# Revit family: 931-20-001 DN250-350
name_source: partatom
category: Pipe Accessories
units: mm (PartAtom-declared; Revit-internal decimal feet)

## family parameters
Always vertical = Yes
Cut with Voids When Loaded = No
Part Type = Valve - Breaks Into
Round Connector Dimension = Use Diameter
Shared = No
Work Plane-Based = No

## types (6) — shared parameters
1 = 1 mm  [stored 0.00328084 ft]
2 = 3 mm  [stored 0.00984252 ft]
DN250 PN10 = 931-250-20-010020200000
DN250 PN16 = 931-250-20-020020200000
DN300_PN10 = 931-300-20-010020200000
DN300_PN16 = 931-300-20-020020200000
DN350_PN10 = 931-350-20-010020200000
DN350_PN16 = 931-350-20-020020200000
Description_ = AVK BUTTERFLY VALVE, LUG, PN10/16
F = 32 mm  [stored 0.104987 ft]
Search_table = 931-20-001 DN250-350
Slot_dim = 19 mm  [stored 0.062336 ft]
URL_product_pages = https://www.avkvalves.com
zero-valued in all types: DISK, Default Elevation

## per-type parameters (varying)
- DN250 PN10: Actuator_FL_T=22 mm  [stored 0.0721785 ft]; Actuator_Flange_R=63 mm; B=125 mm; B1=126 mm; Body_Thickness=8 mm  [stored 0.0262467 ft]; Body_dim=31 mm  [stored 0.101706 ft]; Body_dim1=48 mm  [stored 0.15748 ft]; Body_thickness=132 mm; Bore_R=125 mm; C=68 mm  [stored 0.223097 ft]; D=165 mm; DN=250 mm; E=273 mm; Flange_R=200 mm; Flange_T=22 mm  [stored 0.0721785 ft]; G=22 mm  [stored 0.0721785 ft]; H=75 mm  [stored 0.246063 ft]; Hole=24 mm; Hole1=19 mm  [stored 0.062336 ft]; PCD_R=175 mm; base=24 mm; base1=14 mm  [stored 0.0459318 ft]; base_dis=195 mm; disk=11 mm  [stored 0.0360892 ft]; disk1=22 mm  [stored 0.0721785 ft]; disk11=29 mm  [stored 0.0951444 ft]; disk2=250 mm; disk22=14 mm  [stored 0.0459318 ft]; hole1=11 mm  [stored 0.0360892 ft]; logo=175 mm; rubber=20 mm  [stored 0.0656168 ft]; support=210 mm; wafer=94 mm; wafer_F=28 mm  [stored 0.0918635 ft]; wafer_dim1=31 mm  [stored 0.101706 ft]; wafer_dim2=86 mm  [stored 0.282152 ft]; wafer_fillet=47 mm
- DN250 PN16: Actuator_FL_T=20 mm  [stored 0.0656168 ft]; Actuator_Flange_R=63 mm; B=125 mm; B1=126 mm; Body_Thickness=8 mm  [stored 0.0262467 ft]; Body_dim=31 mm  [stored 0.101706 ft]; Body_dim1=48 mm  [stored 0.15748 ft]; Body_thickness=132 mm; Bore_R=125 mm; C=68 mm  [stored 0.223097 ft]; D=165 mm; DN=250 mm; E=273 mm; Flange_R=200 mm; Flange_T=20 mm  [stored 0.0656168 ft]; G=22 mm  [stored 0.0721785 ft]; H=75 mm  [stored 0.246063 ft]; Hole=24 mm; Hole1=19 mm  [stored 0.062336 ft]; PCD_R=178 mm; base=24 mm; base1=14 mm  [stored 0.0459318 ft]; base_dis=195 mm; disk=12 mm  [stored 0.0393701 ft]; disk1=22 mm  [stored 0.0721785 ft]; disk11=29 mm  [stored 0.0951444 ft]; disk2=250 mm; disk22=16 mm  [stored 0.0524934 ft]; hole1=11 mm  [stored 0.0360892 ft]; logo=175 mm; rubber=20 mm  [stored 0.0656168 ft]; support=210 mm; wafer=94 mm; wafer_F=28 mm  [stored 0.0918635 ft]; wafer_dim1=32 mm  [stored 0.104987 ft]; wafer_dim2=78 mm  [stored 0.255906 ft]; wafer_fillet=47 mm
- DN300_PN10: Actuator_FL_T=20 mm  [stored 0.0656168 ft]; Actuator_Flange_R=63 mm; B=150 mm; B1=151 mm; Body_Thickness=8 mm  [stored 0.0262467 ft]; Body_dim=31 mm  [stored 0.101706 ft]; Body_dim1=55 mm  [stored 0.180446 ft]; Body_thickness=159 mm; Bore_R=150 mm; C=78 mm  [stored 0.255906 ft]; D=188 mm; DN=300 mm; E=311 mm; Flange_R=228 mm; Flange_T=25 mm  [stored 0.082021 ft]; G=22 mm  [stored 0.0721785 ft]; H=75 mm  [stored 0.246063 ft]; Hole=24 mm; Hole1=21 mm  [stored 0.0688976 ft]; PCD_R=200 mm; base=27 mm  [stored 0.0885827 ft]; base1=16 mm  [stored 0.0524934 ft]; base_dis=222 mm; disk=12 mm  [stored 0.0393701 ft]; disk1=22 mm  [stored 0.0721785 ft]; disk11=29 mm  [stored 0.0951444 ft]; disk2=300 mm; disk22=16 mm  [stored 0.0524934 ft]; hole1=11 mm  [stored 0.0360892 ft]; logo=198 mm; rubber=19 mm  [stored 0.062336 ft]; support=238 mm; wafer=94 mm; wafer_F=29 mm  [stored 0.0951444 ft]; wafer_dim1=38 mm  [stored 0.124672 ft]; wafer_dim2=90 mm  [stored 0.295276 ft]; wafer_fillet=47 mm
- DN300_PN16: Actuator_FL_T=20 mm  [stored 0.0656168 ft]; Actuator_Flange_R=63 mm; B=150 mm; B1=151 mm; Body_Thickness=8 mm  [stored 0.0262467 ft]; Body_dim=31 mm  [stored 0.101706 ft]; Body_dim1=55 mm  [stored 0.180446 ft]; Body_thickness=159 mm; Bore_R=150 mm; C=78 mm  [stored 0.255906 ft]; D=188 mm; DN=300 mm; E=311 mm; Flange_R=228 mm; Flange_T=25 mm  [stored 0.082021 ft]; G=22 mm  [stored 0.0721785 ft]; H=75 mm  [stored 0.246063 ft]; Hole=24 mm; Hole1=21 mm  [stored 0.0688976 ft]; PCD_R=205 mm; base=27 mm  [stored 0.0885827 ft]; base1=16 mm  [stored 0.0524934 ft]; base_dis=222 mm; disk=12 mm  [stored 0.0393701 ft]; disk1=23 mm  [stored 0.0754593 ft]; disk11=30 mm  [stored 0.0984252 ft]; disk2=300 mm; disk22=16 mm  [stored 0.0524934 ft]; hole1=11 mm  [stored 0.0360892 ft]; logo=198 mm; rubber=19 mm  [stored 0.062336 ft]; support=238 mm; wafer=94 mm; wafer_F=29 mm  [stored 0.0951444 ft]; wafer_dim1=40 mm  [stored 0.131234 ft]; wafer_dim2=85 mm  [stored 0.278871 ft]; wafer_fillet=47 mm
- DN350_PN10: Actuator_FL_T=20 mm  [stored 0.0656168 ft]; Actuator_Flange_R=75 mm  [stored 0.246063 ft]; B=174 mm; B1=175 mm; Body_Thickness=2 mm  [stored 0.00656168 ft]; Body_dim=38 mm  [stored 0.124672 ft]; Body_dim1=55 mm  [stored 0.180446 ft]; Body_thickness=184 mm; Bore_R=175 mm; C=78 mm  [stored 0.255906 ft]; D=213 mm; DN=350 mm; E=306 mm; Flange_R=200 mm; Flange_T=25 mm  [stored 0.082021 ft]; G=27 mm  [stored 0.0885827 ft]; H=88 mm; Hole=30 mm  [stored 0.0984252 ft]; Hole1=24 mm; PCD_R=230 mm; base=27 mm  [stored 0.0885827 ft]; base1=16 mm  [stored 0.0524934 ft]; base_dis=251 mm; disk=15 mm  [stored 0.0492126 ft]; disk1=27 mm  [stored 0.0885827 ft]; disk11=35 mm  [stored 0.114829 ft]; disk2=348 mm; disk22=20 mm  [stored 0.0656168 ft]; hole1=14 mm  [stored 0.0459318 ft]; logo=223 mm; rubber=19 mm  [stored 0.062336 ft]; support=248 mm; wafer=113 mm; wafer_F=40 mm  [stored 0.131234 ft]; wafer_dim1=25 mm  [stored 0.082021 ft]; wafer_dim2=113 mm; wafer_fillet=56 mm  [stored 0.183727 ft]
- DN350_PN16: Actuator_FL_T=20 mm  [stored 0.0656168 ft]; Actuator_Flange_R=75 mm  [stored 0.246063 ft]; B=174 mm; B1=175 mm; Body_Thickness=2 mm  [stored 0.00656168 ft]; Body_dim=38 mm  [stored 0.124672 ft]; Body_dim1=55 mm  [stored 0.180446 ft]; Body_thickness=184 mm; Bore_R=175 mm; C=78 mm  [stored 0.255906 ft]; D=213 mm; DN=350 mm; E=306 mm; Flange_R=200 mm; Flange_T=27 mm  [stored 0.0885827 ft]; G=27 mm  [stored 0.0885827 ft]; H=88 mm; Hole=30 mm  [stored 0.0984252 ft]; Hole1=24 mm; PCD_R=235 mm; base=27 mm  [stored 0.0885827 ft]; base1=16 mm  [stored 0.0524934 ft]; base_dis=251 mm; disk=15 mm  [stored 0.0492126 ft]; disk1=27 mm  [stored 0.0885827 ft]; disk11=35 mm  [stored 0.114829 ft]; disk2=348 mm; disk22=20 mm  [stored 0.0656168 ft]; hole1=14 mm  [stored 0.0459318 ft]; logo=223 mm; rubber=19 mm  [stored 0.062336 ft]; support=248 mm; wafer=113 mm; wafer_F=40 mm  [stored 0.131234 ft]; wafer_dim1=27 mm  [stored 0.0885827 ft]; wafer_dim2=113 mm; wafer_fillet=56 mm  [stored 0.183727 ft]

note: [stored X ft] marks values corroborated as IEEE doubles in the binary element streams (Revit-internal decimal feet)

## geometry (parser evidence)
native form markers: Sweep x5
no freeform markers — native parametric forms only
